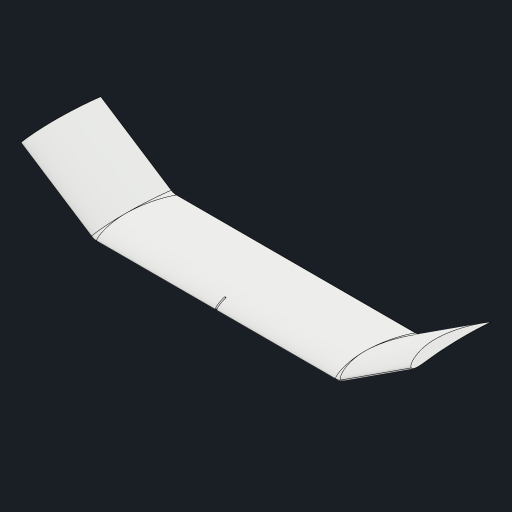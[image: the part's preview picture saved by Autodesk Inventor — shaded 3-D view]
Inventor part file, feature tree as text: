
AUTODESK INVENTOR PART (.ipt)
format: ipt  version: 2023 (Build 270158000, 158)  size: 274,432 bytes
history: native  units: mm
features: sketch x4, extrude x3, other x2, projected_geometry x2, revolve x1, mirror x1
ambient origin geometry x8: Origin, YZ Plane, XZ Plane, XY Plane, X Axis, Y Axis, Z Axis, Center Point
bodies: Body1 (feature_tree)
feature tree (13):
  other  "ソリッド1"
  extrude  "押し出し1"  Depth=270.0mm TaperAngle=0.0deg
  revolve  "回転1"
  extrude  "押し出し3"  Depth=5.759587mm
  mirror  "ミラー4"
  extrude  "押し出し4"  Depth=180.0mm
  sketch  "スケッチ1"
  sketch  "スケッチ7"
  projected_geometry  "投影ループ2"
  sketch  "スケッチ9"
  projected_geometry  "投影ループ4"
  sketch  "スケッチ11"
  other  "断面エッジを投影3"
